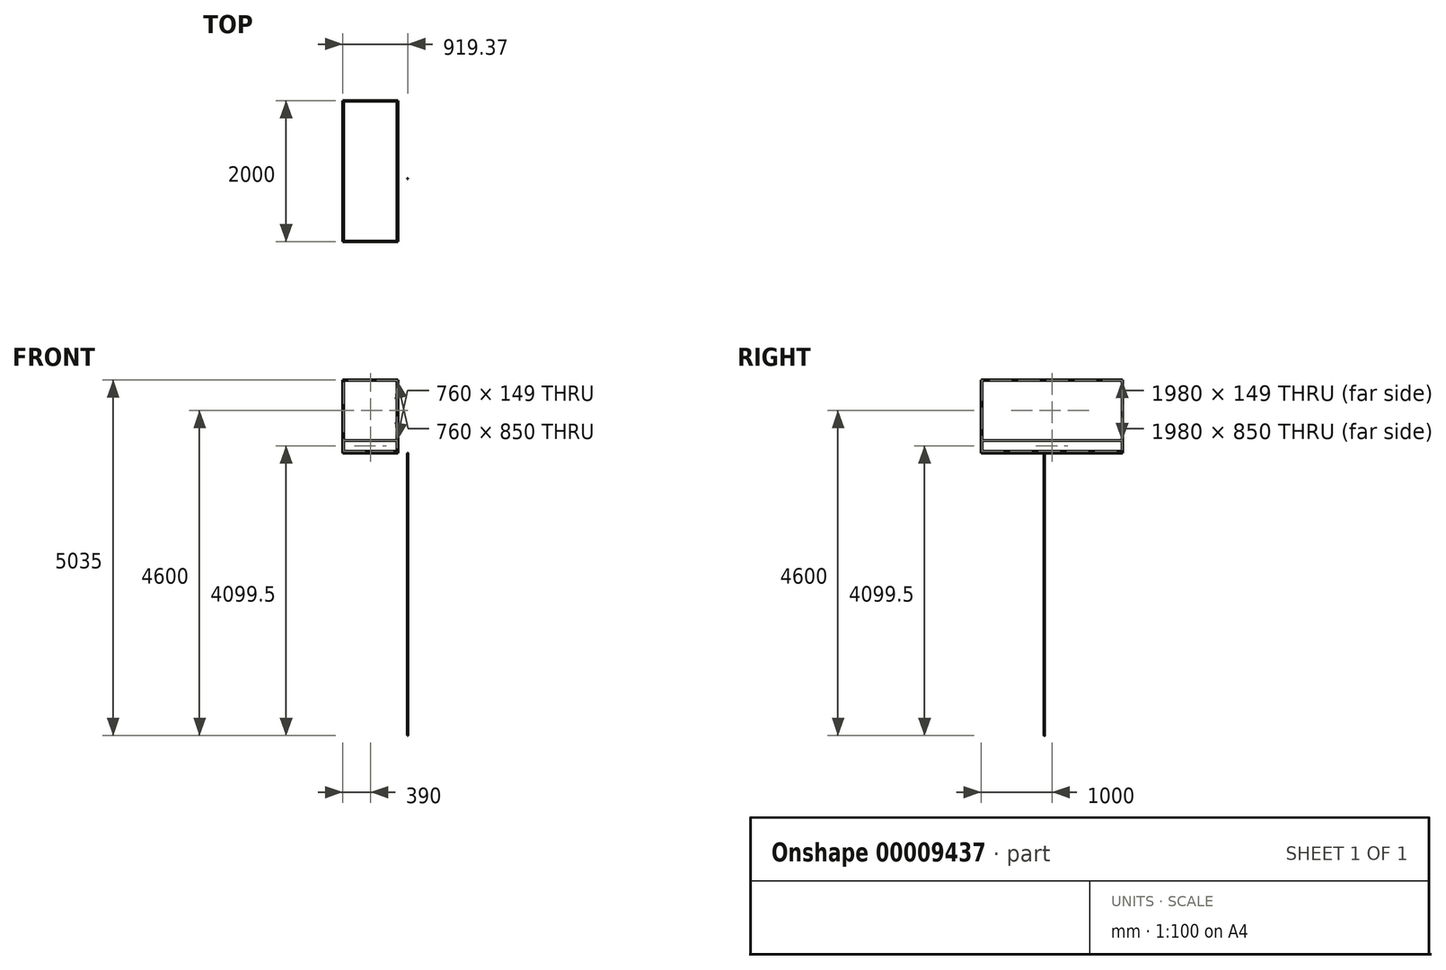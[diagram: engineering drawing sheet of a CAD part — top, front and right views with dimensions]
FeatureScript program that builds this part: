
annotation { "Feature Type Name" : "Feature", "Feature Type Description" : "" }
export const myFeature = defineFeature(function(context is Context, id is Id, definition is map)
    precondition{}
    {
        {
            var Q0;
            Q0=qCreatedBy(makeId("Top.planeOp"),FACE);
            var sketch = newSketch(context, id + "F0", { "sketchPlane" : qUnion([Q0])});
            skLineSegment(sketch, "E0.rect.bottom", {"start": v(390, -1000) * mm, "end": v(-390, -1000) * mm});
            skLineSegment(sketch, "E0.rect.top", {"start": v(390, 1000) * mm, "end": v(-390, 1000) * mm});
            skLineSegment(sketch, "E0.rect.left", {"start": v(390, -1000) * mm, "end": v(390, 1000) * mm});
            skLineSegment(sketch, "E0.rect.right", {"start": v(-390, -1000) * mm, "end": v(-390, 1000) * mm});
            skPoint(sketch, "E0.rect.middle", {"position": v(0, 0) * mm});
            skSolve(sketch);
        }
        {
            var Q0;
            Q0=makeQuery(id+"F0.imprint","IMPRINT",FACE,{"disambiguationData":[TD([[makeQuery(id+"F0.imprint","IMPRINT",EDGE,{"derivedFrom":sQuery(id+"F0.wireOp",EDGE,"E0.rect.bottom")}),-1.0]])]});
            extrude(context, id + "F1", {"entities" : qUnion([Q0]), "depth" : 25 * mm});
        }
        {
            var Q0;
            Q0=makeQuery(id+"F1.opExtrude","CAP_FACE",FACE,{"disambiguationData":[OSD([sQuery(id+"F0.wireOp",EDGE,"E0.rect.bottom"),sQuery(id+"F0.wireOp",EDGE,"E0.rect.top"),sQuery(id+"F0.wireOp",EDGE,"E0.rect.left"),sQuery(id+"F0.wireOp",EDGE,"E0.rect.right")])],"isStart":false});
            var sketch = newSketch(context, id + "F2", { "sketchPlane" : qUnion([Q0])});
            skLineSegment(sketch, "E1.bottom", {"start": v(-390, -1000) * mm, "end": v(-380, -1000) * mm});
            skLineSegment(sketch, "E1.top", {"start": v(-390, -990) * mm, "end": v(-380, -990) * mm});
            skLineSegment(sketch, "E1.left", {"start": v(-390, -1000) * mm, "end": v(-390, -990) * mm});
            skLineSegment(sketch, "E1.right", {"start": v(-380, -1000) * mm, "end": v(-380, -990) * mm});
            skLineSegment(sketch, "E2.bottom", {"start": v(390, -1000) * mm, "end": v(380, -1000) * mm});
            skLineSegment(sketch, "E2.top", {"start": v(390, -990) * mm, "end": v(380, -990) * mm});
            skLineSegment(sketch, "E2.left", {"start": v(390, -1000) * mm, "end": v(390, -990) * mm});
            skLineSegment(sketch, "E2.right", {"start": v(380, -1000) * mm, "end": v(380, -990) * mm});
            skLineSegment(sketch, "E3.bottom", {"start": v(390, 1000) * mm, "end": v(380, 1000) * mm});
            skLineSegment(sketch, "E3.top", {"start": v(390, 990) * mm, "end": v(380, 990) * mm});
            skLineSegment(sketch, "E3.left", {"start": v(390, 1000) * mm, "end": v(390, 990) * mm});
            skLineSegment(sketch, "E3.right", {"start": v(380, 1000) * mm, "end": v(380, 990) * mm});
            skLineSegment(sketch, "E4.bottom", {"start": v(-390, 1000) * mm, "end": v(-380, 1000) * mm});
            skLineSegment(sketch, "E4.top", {"start": v(-390, 990) * mm, "end": v(-380, 990) * mm});
            skLineSegment(sketch, "E4.left", {"start": v(-390, 1000) * mm, "end": v(-390, 990) * mm});
            skLineSegment(sketch, "E4.right", {"start": v(-380, 1000) * mm, "end": v(-380, 990) * mm});
            skSolve(sketch);
        }
        {
            var Q0;
            Q0 = qSketchRegion(id + "F2", true);
            extrude(context, id + "F3", {"entities" : qUnion([Q0]), "operationType" : NewBodyOperationType.ADD, "depth" : 1000 * mm});
        }
        {
            var Q0;
            Q0=makeQuery(id+"F3.opExtrude","CAP_FACE",FACE,{"disambiguationData":[OSD([sQuery(id+"F2.wireOp",EDGE,"E1.bottom"),sQuery(id+"F2.wireOp",EDGE,"E1.top"),sQuery(id+"F2.wireOp",EDGE,"E1.left"),sQuery(id+"F2.wireOp",EDGE,"E1.right")])],"isStart":false});
            var sketch = newSketch(context, id + "F4", { "sketchPlane" : qUnion([Q0])});
            skLineSegment(sketch, "E5.bottom", {"start": v(-390, -1000) * mm, "end": v(-380, -1000) * mm});
            skLineSegment(sketch, "E5.top", {"start": v(-390, 1000) * mm, "end": v(-380, 1000) * mm});
            skLineSegment(sketch, "E5.left", {"start": v(-390, -1000) * mm, "end": v(-390, 1000) * mm});
            skLineSegment(sketch, "E5.right", {"start": v(-380, -1000) * mm, "end": v(-380, 1000) * mm});
            skLineSegment(sketch, "E6.bottom", {"start": v(390, -1000) * mm, "end": v(380, -1000) * mm});
            skLineSegment(sketch, "E6.top", {"start": v(390, 1000) * mm, "end": v(380, 1000) * mm});
            skLineSegment(sketch, "E6.left", {"start": v(390, -1000) * mm, "end": v(390, 1000) * mm});
            skLineSegment(sketch, "E6.right", {"start": v(380, -1000) * mm, "end": v(380, 1000) * mm});
            skLineSegment(sketch, "E7.bottom", {"start": v(380, 1000) * mm, "end": v(-380, 1000) * mm});
            skLineSegment(sketch, "E7.top", {"start": v(380, 990) * mm, "end": v(-380, 990) * mm});
            skLineSegment(sketch, "E7.left", {"start": v(380, 1000) * mm, "end": v(380, 990) * mm});
            skLineSegment(sketch, "E7.right", {"start": v(-380, 1000) * mm, "end": v(-380, 990) * mm});
            skLineSegment(sketch, "E8.bottom", {"start": v(380, -1000) * mm, "end": v(-380, -1000) * mm});
            skLineSegment(sketch, "E8.top", {"start": v(380, -990) * mm, "end": v(-380, -990) * mm});
            skLineSegment(sketch, "E8.left", {"start": v(380, -1000) * mm, "end": v(380, -990) * mm});
            skLineSegment(sketch, "E8.right", {"start": v(-380, -1000) * mm, "end": v(-380, -990) * mm});
            skSolve(sketch);
        }
        {
            var Q0;
            Q0 = qSketchRegion(id + "F4", true);
            extrude(context, id + "F5", {"entities" : qUnion([Q0]), "operationType" : NewBodyOperationType.ADD, "depth" : 10 * mm});
        }
        {
            var Q0;
            Q0=makeQuery(id+"F1.opExtrude","CAP_FACE",FACE,{"disambiguationData":[OSD([sQuery(id+"F0.wireOp",EDGE,"E0.rect.bottom"),sQuery(id+"F0.wireOp",EDGE,"E0.rect.top"),sQuery(id+"F0.wireOp",EDGE,"E0.rect.left"),sQuery(id+"F0.wireOp",EDGE,"E0.rect.right")])],"isStart":false});
            extrude(context, id + "F6", {"entities" : qUnion([Q0]), "operationType" : NewBodyOperationType.ADD, "depth" : 150 * mm, "hasSecondDirection" : true, "secondDirectionOppositeDirection" : false, "secondDirectionDepth" : 149 * mm});
        }
        {
            var Q0;
            Q0=makeQuery(id+"F1.opExtrude","CAP_FACE",FACE,{"disambiguationData":[OSD([sQuery(id+"F0.wireOp",EDGE,"E0.rect.bottom"),sQuery(id+"F0.wireOp",EDGE,"E0.rect.top"),sQuery(id+"F0.wireOp",EDGE,"E0.rect.left"),sQuery(id+"F0.wireOp",EDGE,"E0.rect.right")])],"isStart":true});
            var sketch = newSketch(context, id + "F7", { "sketchPlane" : qUnion([Q0])});
            skCircle(sketch, "E9", {"center": v(526.87, 106.95) * mm, "radius": 2.5 * mm});
            skSolve(sketch);
        }
        {
            var Q0;
            Q0=makeQuery(id+"F7.imprint","IMPRINT",FACE,{"disambiguationData":[TD([[makeQuery(id+"F7.imprint","IMPRINT",EDGE,{"derivedFrom":sQuery(id+"F7.wireOp",EDGE,"E9")}),1.0]])]});
            extrude(context, id + "F8", {"entities" : qUnion([Q0]), "depth" : 4000 * mm});
        }
        {
            var Q0;
            Q0 = qSketchRegion(id + "F7", true);
            extrude(context, id + "F9", {"entities" : qUnion([Q0]), "depth" : 2000 * mm});
        }
    });
